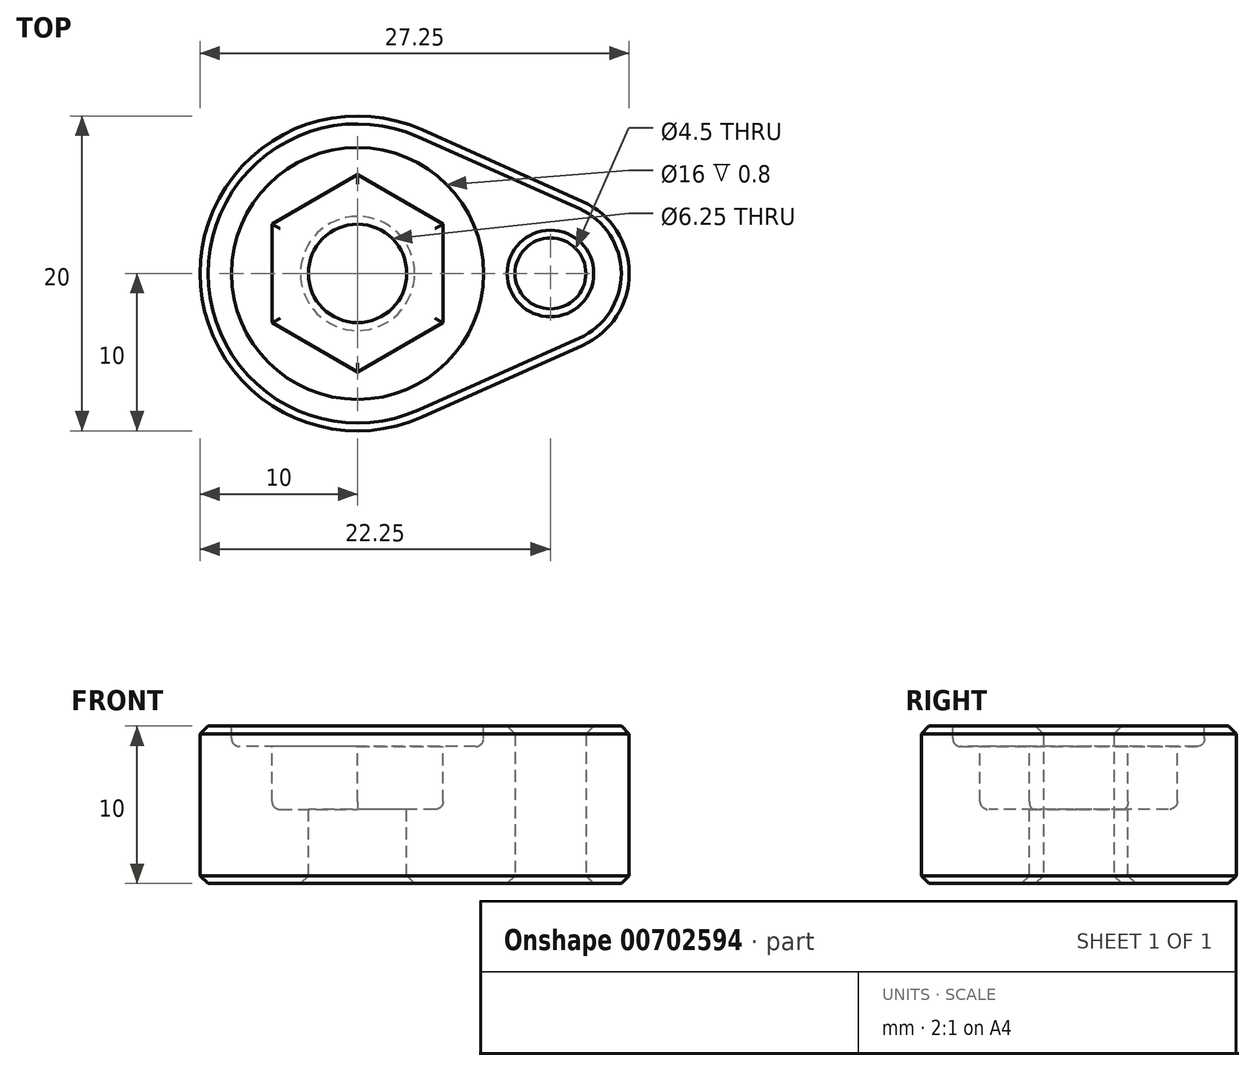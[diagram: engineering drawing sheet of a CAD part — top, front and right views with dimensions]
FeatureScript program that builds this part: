
annotation { "Feature Type Name" : "Feature", "Feature Type Description" : "" }
export const myFeature = defineFeature(function(context is Context, id is Id, definition is map)
    precondition{}
    {
        {
            var Q0;
            Q0=qCreatedBy(makeId("Top.planeOp"),FACE);
            var sketch = newSketch(context, id + "F0", { "sketchPlane" : qUnion([Q0])});
            skArc(sketch, "E0", {"start": v(4.08, 9.13) * mm, "mid": v(-10, 0) * mm, "end": v(4.08, -9.13) * mm});
            skCircle(sketch, "E1", {"center": v(12.25, 0) * mm, "radius": 2.25 * mm});
            skArc(sketch, "E2", {"start": v(14.3, -4.56) * mm, "mid": v(17.25, 0) * mm, "end": v(14.3, 4.56) * mm});
            skLineSegment(sketch, "E3", {"start": v(4.08, 9.13) * mm, "end": v(14.3, 4.56) * mm});
            skLineSegment(sketch, "E4", {"start": v(4.08, -9.13) * mm, "end": v(14.3, -4.56) * mm});
            skSolve(sketch);
        }
        {
            var Q0;
            Q0=makeQuery(id+"F0.imprint","IMPRINT",FACE,{"disambiguationData":[TD([[makeQuery(id+"F0.imprint","IMPRINT",EDGE,{"derivedFrom":sQuery(id+"F0.wireOp",EDGE,"E0")}),1.0]])]});
            extrude(context, id + "F1", {"entities" : qUnion([Q0]), "depth" : 10 * mm, "offsetDistance" : 25 * mm});
        }
        {
            var Q0;
            Q0=makeQuery(id+"F1.opExtrude","CAP_FACE",FACE,{"disambiguationData":[OSD([sQuery(id+"F0.wireOp",EDGE,"E0"),sQuery(id+"F0.wireOp",EDGE,"E1"),sQuery(id+"F0.wireOp",EDGE,"E2"),sQuery(id+"F0.wireOp",EDGE,"E3"),sQuery(id+"F0.wireOp",EDGE,"E4")])],"isStart":false});
            var sketch = newSketch(context, id + "F2", { "sketchPlane" : qUnion([Q0])});
            skCircle(sketch, "E5", {"center": v(0, 0) * mm, "radius": 8 * mm});
            skSolve(sketch);
        }
        {
            var Q0;
            Q0=makeQuery(id+"F2.imprint","IMPRINT",FACE,{"disambiguationData":[TD([[makeQuery(id+"F2.imprint","IMPRINT",EDGE,{"derivedFrom":sQuery(id+"F2.wireOp",EDGE,"E5")}),1.0]])]});
            extrude(context, id + "F3", {"entities" : qUnion([Q0]), "operationType" : NewBodyOperationType.REMOVE, "oppositeDirection" : true, "depth" : 1.3 * mm, "offsetDistance" : 25 * mm});
        }
        {
            var Q0;
            Q0=makeQuery(id+"F3.boolean.opBoolean","COPY",FACE,{"derivedFrom":makeQuery(id+"F3.opExtrude","CAP_FACE",FACE,{"disambiguationData":[OSD([sQuery(id+"F2.wireOp",EDGE,"E5")])],"isStart":false})});
            var sketch = newSketch(context, id + "F4", { "sketchPlane" : qUnion([Q0])});
            skCircle(sketch, "E6.cCircle", {"center": v(0, 0) * mm, "radius": 5.43 * mm, "construction": true});
            skLineSegment(sketch, "E6.0", {"start": v(5.43, 3.13) * mm, "end": v(5.43, -3.13) * mm});
            skLineSegment(sketch, "E6.1", {"start": v(5.43, -3.13) * mm, "end": v(0, -6.26) * mm});
            skLineSegment(sketch, "E6.2", {"start": v(0, -6.26) * mm, "end": v(-5.42, -3.13) * mm});
            skLineSegment(sketch, "E6.3", {"start": v(-5.42, -3.13) * mm, "end": v(-5.43, 3.13) * mm});
            skLineSegment(sketch, "E6.4", {"start": v(-5.43, 3.13) * mm, "end": v(0, 6.26) * mm});
            skLineSegment(sketch, "E6.5", {"start": v(0, 6.26) * mm, "end": v(5.43, 3.13) * mm});
            skPoint(sketch, "E6.0.midPoint", {"position": v(5.43, 0) * mm});
            skSolve(sketch);
        }
        {
            var Q0;
            Q0=makeQuery(id+"F4.imprint","IMPRINT",FACE,{"disambiguationData":[TD([[makeQuery(id+"F4.imprint","IMPRINT",EDGE,{"derivedFrom":sQuery(id+"F4.wireOp",EDGE,"E6.0")}),-1.0]])]});
            extrude(context, id + "F5", {"entities" : qUnion([Q0]), "operationType" : NewBodyOperationType.REMOVE, "oppositeDirection" : true, "depth" : 4 * mm, "offsetDistance" : 25 * mm});
        }
        {
            var Q0;
            Q0=makeQuery(id+"F5.boolean.opBoolean","COPY",FACE,{"derivedFrom":makeQuery(id+"F5.opExtrude","CAP_FACE",FACE,{"disambiguationData":[OSD([sQuery(id+"F4.wireOp",EDGE,"E6.0"),sQuery(id+"F4.wireOp",EDGE,"E6.1"),sQuery(id+"F4.wireOp",EDGE,"E6.2"),sQuery(id+"F4.wireOp",EDGE,"E6.3"),sQuery(id+"F4.wireOp",EDGE,"E6.4"),sQuery(id+"F4.wireOp",EDGE,"E6.5")])],"isStart":false})});
            var sketch = newSketch(context, id + "F6", { "sketchPlane" : qUnion([Q0])});
            skCircle(sketch, "E7", {"center": v(0, 0) * mm, "radius": 3.12 * mm});
            skSolve(sketch);
        }
        {
            var Q0;
            Q0=makeQuery(id+"F6.imprint","IMPRINT",FACE,{"disambiguationData":[TD([[makeQuery(id+"F6.imprint","IMPRINT",EDGE,{"derivedFrom":sQuery(id+"F6.wireOp",EDGE,"E7")}),1.0]])]});
            extrude(context, id + "F7", {"entities" : qUnion([Q0]), "operationType" : NewBodyOperationType.REMOVE, "endBound" : BoundingType.THROUGH_ALL, "oppositeDirection" : true, "depth" : 25 * mm, "offsetDistance" : 25 * mm});
        }
        {
            var Q0;
            Q0=makeQuery(id+"F3.boolean.opBoolean","COPY",EDGE,{"derivedFrom":makeQuery(id+"F3.opExtrude","CAP_EDGE",EDGE,{"disambiguationData":[OSD([sQuery(id+"F2.wireOp",EDGE,"E5")])],"isStart":false})});
            var Q1;
            Q1=makeQuery(id+"F5.boolean.opBoolean","COPY",EDGE,{"derivedFrom":makeQuery(id+"F5.opExtrude","CAP_EDGE",EDGE,{"disambiguationData":[OSD([sQuery(id+"F4.wireOp",EDGE,"E6.4")])],"isStart":false})});
            var Q2;
            Q2=makeQuery(id+"F5.boolean.opBoolean","COPY",EDGE,{"derivedFrom":makeQuery(id+"F5.opExtrude","CAP_EDGE",EDGE,{"disambiguationData":[OSD([sQuery(id+"F4.wireOp",EDGE,"E6.5")])],"isStart":false})});
            var Q3;
            Q3=makeQuery(id+"F5.boolean.opBoolean","COPY",EDGE,{"derivedFrom":makeQuery(id+"F5.opExtrude","CAP_EDGE",EDGE,{"disambiguationData":[OSD([sQuery(id+"F4.wireOp",EDGE,"E6.3")])],"isStart":false})});
            var Q4;
            Q4=makeQuery(id+"F5.boolean.opBoolean","COPY",EDGE,{"derivedFrom":makeQuery(id+"F5.opExtrude","CAP_EDGE",EDGE,{"disambiguationData":[OSD([sQuery(id+"F4.wireOp",EDGE,"E6.2")])],"isStart":false})});
            var Q5;
            Q5=makeQuery(id+"F5.boolean.opBoolean","COPY",EDGE,{"derivedFrom":makeQuery(id+"F5.opExtrude","CAP_EDGE",EDGE,{"disambiguationData":[OSD([sQuery(id+"F4.wireOp",EDGE,"E6.1")])],"isStart":false})});
            var Q6;
            Q6=makeQuery(id+"F5.boolean.opBoolean","COPY",EDGE,{"derivedFrom":makeQuery(id+"F5.opExtrude","CAP_EDGE",EDGE,{"disambiguationData":[OSD([sQuery(id+"F4.wireOp",EDGE,"E6.0")])],"isStart":false})});
            fillet(context, id + "F8", {"entities" : qUnion([Q0, Q1, Q2, Q3, Q4, Q5, Q6]), "radius" : 0.5 * mm, "tangentPropagation" : true, "allowEdgeOverflow" : false});
        }
        {
            var Q0;
            Q0=makeQuery(id+"F3.boolean.opBoolean","COPY",EDGE,{"derivedFrom":makeQuery(id+"F3.opExtrude","CAP_EDGE",EDGE,{"disambiguationData":[OSD([sQuery(id+"F2.wireOp",EDGE,"E5")])],"isStart":true})});
            var Q1;
            Q1=makeQuery(id+"F1.opExtrude","CAP_EDGE",EDGE,{"disambiguationData":[OSD([sQuery(id+"F0.wireOp",EDGE,"E1")])],"isStart":false});
            var Q2;
            Q2=makeQuery(id+"F1.opExtrude","CAP_EDGE",EDGE,{"disambiguationData":[OSD([sQuery(id+"F0.wireOp",EDGE,"E0")])],"isStart":false});
            var Q3;
            Q3=makeQuery(id+"F1.opExtrude","CAP_EDGE",EDGE,{"disambiguationData":[OSD([sQuery(id+"F0.wireOp",EDGE,"E4")])],"isStart":false});
            var Q4;
            Q4=makeQuery(id+"F1.opExtrude","CAP_EDGE",EDGE,{"disambiguationData":[OSD([sQuery(id+"F0.wireOp",EDGE,"E0")])],"isStart":true});
            var Q5;
            Q5=makeQuery(id+"F1.opExtrude","CAP_EDGE",EDGE,{"disambiguationData":[OSD([sQuery(id+"F0.wireOp",EDGE,"E3")])],"isStart":true});
            var Q6;
            Q6=makeQuery(id+"F7.boolean.opBoolean","INTERSECT",EDGE,{"derivedFrom":[makeQuery(id+"F1.opExtrude","CAP_FACE",FACE,{"disambiguationData":[OSD([sQuery(id+"F0.wireOp",EDGE,"E0"),sQuery(id+"F0.wireOp",EDGE,"E1"),sQuery(id+"F0.wireOp",EDGE,"E2"),sQuery(id+"F0.wireOp",EDGE,"E3"),sQuery(id+"F0.wireOp",EDGE,"E4")])],"isStart":true}),makeQuery(id+"F7.opExtrude","SWEPT_FACE",FACE,{"disambiguationData":[OSD([sQuery(id+"F6.wireOp",EDGE,"E7")])]})]});
            var Q7;
            Q7=makeQuery(id+"F1.opExtrude","CAP_EDGE",EDGE,{"disambiguationData":[OSD([sQuery(id+"F0.wireOp",EDGE,"E1")])],"isStart":true});
            var Q8;
            Q8=makeQuery(id+"F7.boolean.opBoolean","COPY",EDGE,{"derivedFrom":makeQuery(id+"F7.opExtrude","CAP_EDGE",EDGE,{"disambiguationData":[OSD([sQuery(id+"F6.wireOp",EDGE,"E7")])],"isStart":true})});
            chamfer(context, id + "F9", {"entities" : qUnion([Q0, Q1, Q2, Q3, Q4, Q5, Q6, Q7, Q8]), "width" : 0.5 * mm, "tangentPropagation" : true});
        }
    });
